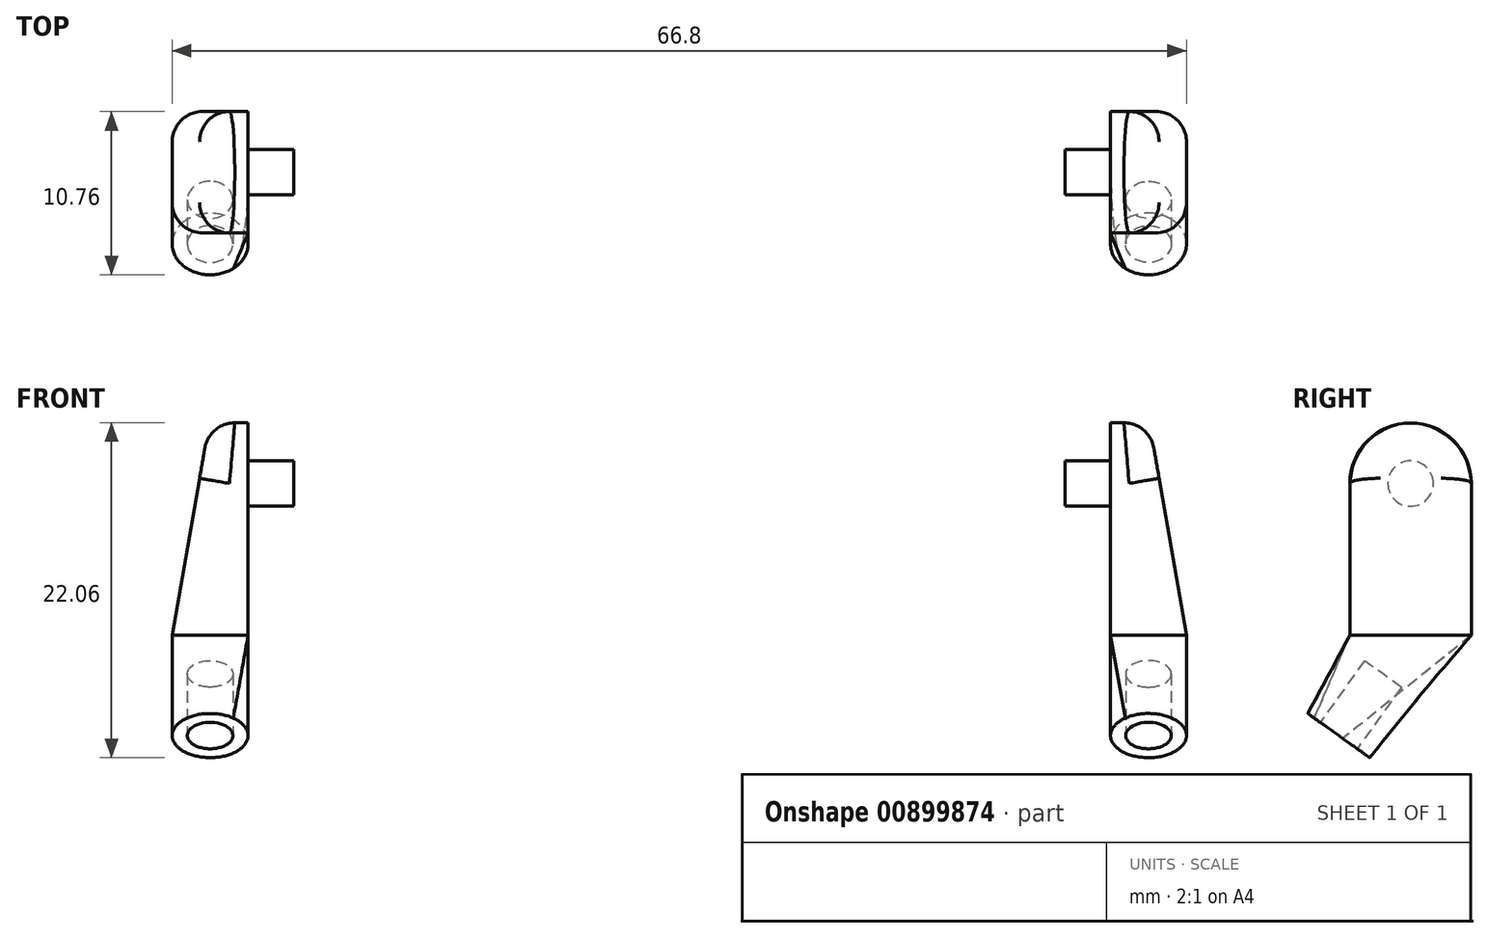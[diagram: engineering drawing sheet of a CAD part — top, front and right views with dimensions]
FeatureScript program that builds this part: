
annotation { "Feature Type Name" : "Feature", "Feature Type Description" : "" }
export const myFeature = defineFeature(function(context is Context, id is Id, definition is map)
    precondition{}
    {
        {
            var Q0;
            Q0=qCreatedBy(makeId("Right.planeOp"),FACE);
            var sketch = newSketch(context, id + "F0", { "sketchPlane" : qUnion([Q0])});
            skCircle(sketch, "E0", {"center": v(0, 0) * mm, "radius": 1.5 * mm});
            skSolve(sketch);
        }
        {
            var Q0;
            Q0 = qSketchRegion(id + "F0", true);
            extrude(context, id + "F1", {"entities" : qUnion([Q0]), "depth" : 3 * mm, "offsetDistance" : 25.4 * mm});
        }
        {
            var Q0;
            Q0=makeQuery(id+"F1.opExtrude","CAP_FACE",FACE,{"disambiguationData":[OSD([sQuery(id+"F0.wireOp",EDGE,"E0")])],"isStart":false});
            var sketch = newSketch(context, id + "F2", { "sketchPlane" : qUnion([Q0])});
            skArc(sketch, "E1", {"start": v(4, 0) * mm, "mid": v(0, 4) * mm, "end": v(-4, 0) * mm});
            skLineSegment(sketch, "E2.top", {"start": v(-4, -10) * mm, "end": v(4, -10) * mm});
            skLineSegment(sketch, "E2.left", {"start": v(-4, 0) * mm, "end": v(-4, -10) * mm});
            skLineSegment(sketch, "E2.right", {"start": v(4, 0) * mm, "end": v(4, -10) * mm});
            skPoint(sketch, "E2.middle", {"position": v(0, -5) * mm});
            skLineSegment(sketch, "E3", {"start": v(4, -10) * mm, "end": v(-2.09, -18.5) * mm, "construction": true});
            skLineSegment(sketch, "E4", {"start": v(-2.09, -18.5) * mm, "end": v(-7.38, -14.72) * mm, "construction": true});
            skLineSegment(sketch, "E5", {"start": v(-7.38, -14.72) * mm, "end": v(-4, -10) * mm, "construction": true});
            skLineSegment(sketch, "E6", {"start": v(-4.73, -16.6) * mm, "end": v(-2.41, -13.37) * mm, "construction": true});
            skSolve(sketch);
        }
        {
            var Q0;
            Q0 = qSketchRegion(id + "F2", true);
            extrude(context, id + "F3", {"entities" : qUnion([Q0]), "operationType" : NewBodyOperationType.ADD, "depth" : 5 * mm, "offsetDistance" : 25.4 * mm});
        }
        {
            var Q0;
            Q0=makeQuery(id+"F3.opExtrude","SWEPT_FACE",FACE,{"disambiguationData":[OSD([sQuery(id+"F2.wireOp",EDGE,"E2.left")])]});
            var sketch = newSketch(context, id + "F4", { "sketchPlane" : qUnion([Q0])});
            skLineSegment(sketch, "E7", {"start": v(8, -10) * mm, "end": v(5.43, 4.75) * mm});
            skLineSegment(sketch, "E8", {"start": v(5.43, 4.75) * mm, "end": v(9.72, 4.75) * mm});
            skLineSegment(sketch, "E9", {"start": v(9.72, 4.75) * mm, "end": v(8, -10) * mm});
            skSolve(sketch);
        }
        {
            var Q0;
            Q0 = qSketchRegion(id + "F4", true);
            extrude(context, id + "F5", {"entities" : qUnion([Q0]), "operationType" : NewBodyOperationType.REMOVE, "oppositeDirection" : true, "depth" : 25 * mm, "offsetDistance" : 25.4 * mm});
        }
        {
            var Q0;
            Q0=makeQuery(id+"F5.boolean.opBoolean","COPY",EDGE,{"derivedFrom":makeQuery(id+"F5.opExtrude","CAP_EDGE",EDGE,{"disambiguationData":[OSD([sQuery(id+"F4.wireOp",EDGE,"E7")])],"isStart":true})});
            var Q1;
            Q1=makeQuery(id+"F5.boolean.opBoolean","INTERSECT",EDGE,{"derivedFrom":[makeQuery(id+"F3.opExtrude","SWEPT_FACE",FACE,{"disambiguationData":[OSD([sQuery(id+"F2.wireOp",EDGE,"E1")])]}),makeQuery(id+"F5.opExtrude","SWEPT_FACE",FACE,{"disambiguationData":[OSD([sQuery(id+"F4.wireOp",EDGE,"E7")])]})]});
            fillet(context, id + "F6", {"entities" : qUnion([Q0, Q1]), "radius" : 2 * mm, "tangentPropagation" : true, "allowEdgeOverflow" : false});
        }
        {
            var Q0;
            Q0=sQuery(id+"F2.wireOp",EDGE,"E5");
            var Q1;
            Q1=sQuery(id+"F2.wireOp",VERTEX,"E4.end");
            cPlane(context, id + "F7", {"entities" : qUnion([Q0, Q1]), "cplaneType" : CPlaneType.LINE_POINT, "offset" : 25.4 * mm, "width" : 152.4 * mm, "height" : 152.4 * mm});
        }
        {
            var Q0;
            Q0=qCreatedBy(id+"F7.planeOp",FACE);
            var sketch = newSketch(context, id + "F8", { "sketchPlane" : qUnion([Q0])});
            skLineSegment(sketch, "E10", {"start": v(3, 5.82) * mm, "end": v(8, 5.82) * mm, "construction": true});
            skCircle(sketch, "E11", {"center": v(5.5, 5.82) * mm, "radius": 2.5 * mm});
            skSolve(sketch);
        }
        {
            var Q1;
            Q1=makeQuery(id+"F3.opExtrude","SWEPT_FACE",FACE,{"disambiguationData":[OSD([sQuery(id+"F2.wireOp",EDGE,"E2.top")])]});
            var Q2;
            Q2=makeQuery(id+"F8.imprint","IMPRINT",FACE,{"disambiguationData":[TD([[makeQuery(id+"F8.imprint","IMPRINT",EDGE,{"derivedFrom":sQuery(id+"F8.wireOp",EDGE,"E11")}),1.0]])]});
            loft(context, id + "F9", {"operationType" : NewBodyOperationType.ADD, "sheetProfilesArray" : [{ "sheetProfileEntities" : qUnion([Q1]) }, { "sheetProfileEntities" : qUnion([Q2]) }]});
        }
        {
            var Q0;
            Q0=makeQuery(id+"F9.opLoft","CAP_FACE",FACE,{"disambiguationData":[OSD([makeQuery(id+"F8.imprint","IMPRINT",FACE,{"disambiguationData":[TD([[makeQuery(id+"F8.imprint","IMPRINT",EDGE,{"derivedFrom":sQuery(id+"F8.wireOp",EDGE,"E11")}),1.0]])]})])],"isStart":true});
            var sketch = newSketch(context, id + "F10", { "sketchPlane" : qUnion([Q0])});
            skCircle(sketch, "E12", {"center": v(5.5, -5.82) * mm, "radius": 1.5 * mm});
            skSolve(sketch);
        }
        {
            var Q0;
            Q0 = qSketchRegion(id + "F10", true);
            extrude(context, id + "F11", {"entities" : qUnion([Q0]), "operationType" : NewBodyOperationType.REMOVE, "oppositeDirection" : true, "depth" : 5 * mm, "offsetDistance" : 25.4 * mm});
        }
        {
            var Q0;
            Q0=makeQuery(id+"F1.opExtrude","SWEPT_BODY",BODY,{"disambiguationData":[OSD([sQuery(id+"F0.wireOp",EDGE,"E0")])]});
            transform(context, id + "F12", {"entities" : qUnion([Q0]), "transformType" : TransformType.TRANSLATION_3D, "dx" : 25.4 * mm, "dy" : 0 * mm, "dz" : 0 * mm, "makeCopy" : true});
        }
        {
            var Q0;
            Q0=makeQuery(id+"F12.opPattern","COPY",BODY,{"derivedFrom":makeQuery(id+"F1.opExtrude","SWEPT_BODY",BODY,{"disambiguationData":[OSD([sQuery(id+"F0.wireOp",EDGE,"E0")])]}),"instanceName":"1"});
            var Q1;
            Q1=qCreatedBy(makeId("Right.planeOp"),FACE);
            mirror(context, id + "F13", {"entities" : qUnion([Q0]), "mirrorPlane" : qUnion([Q1])});
        }
        {
            var Q0;
            Q0=makeQuery(id+"F1.opExtrude","SWEPT_BODY",BODY,{"disambiguationData":[OSD([sQuery(id+"F0.wireOp",EDGE,"E0")])]});
            deleteBodies(context, id + "F14", {"entities" : qUnion([Q0])});
        }
    });
